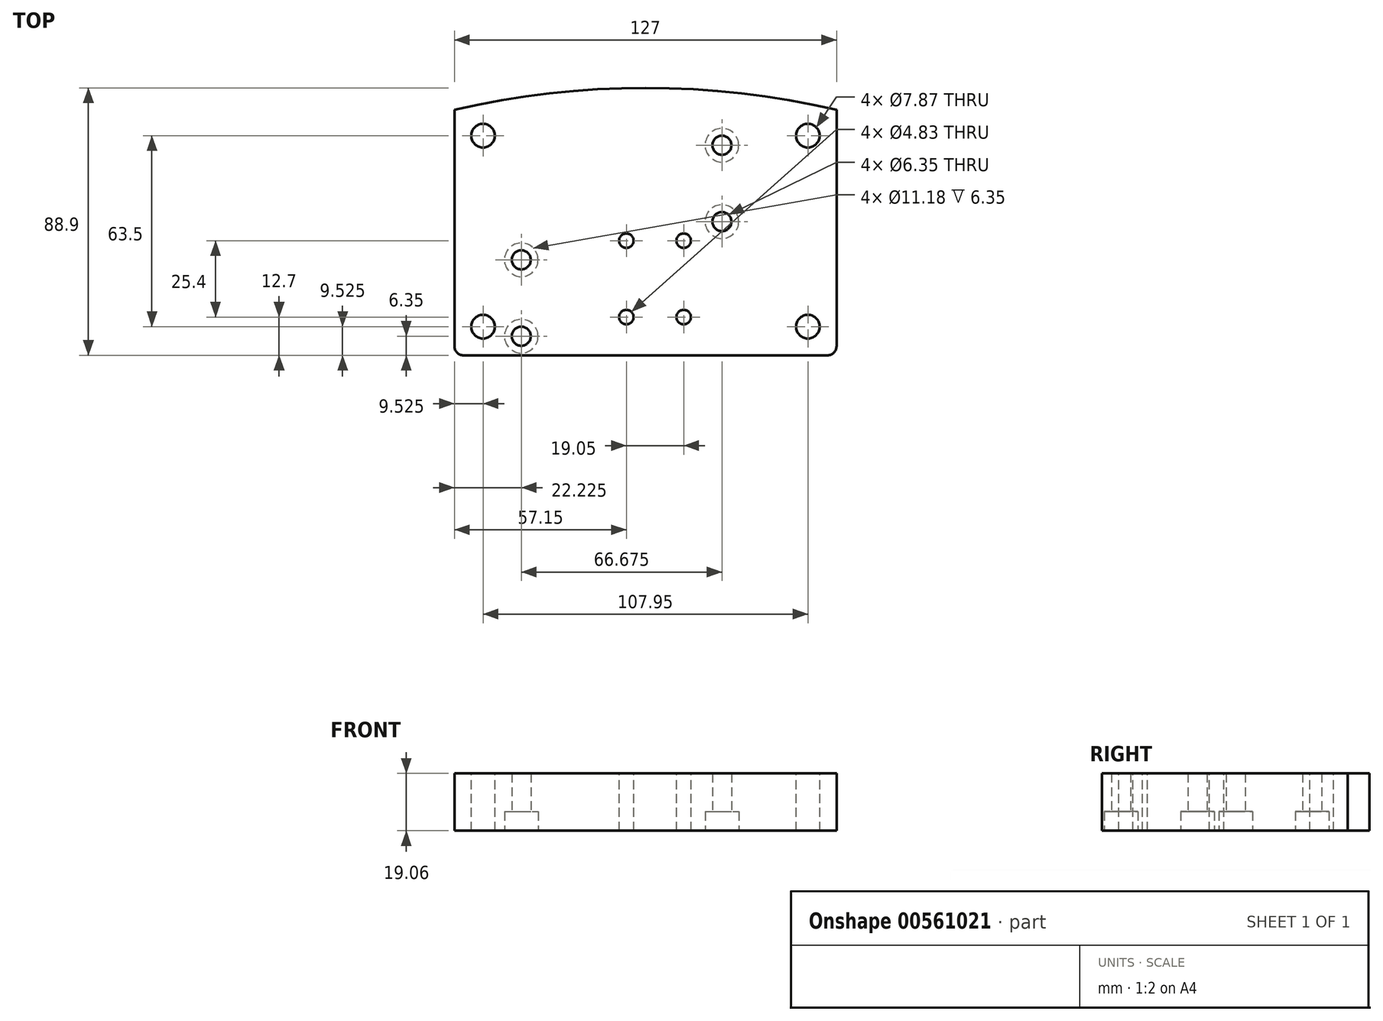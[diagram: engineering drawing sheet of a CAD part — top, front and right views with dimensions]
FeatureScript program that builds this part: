
annotation { "Feature Type Name" : "Feature", "Feature Type Description" : "" }
export const myFeature = defineFeature(function(context is Context, id is Id, definition is map)
    precondition{}
    {
        {
            var Q0;
            Q0=qCreatedBy(makeId("Front.planeOp"),FACE);
            var sketch = newSketch(context, id + "F0", { "sketchPlane" : qUnion([Q0])});
            skLineSegment(sketch, "E0", {"start": v(0, 82.23) * mm, "end": v(0, -82.23) * mm, "construction": true});
            skPoint(sketch, "E1", {"position": v(0, 0) * mm});
            skLineSegment(sketch, "E2.bottom", {"start": v(63.5, -9.52) * mm, "end": v(-63.5, -9.52) * mm});
            skLineSegment(sketch, "E2.top", {"start": v(63.5, 9.53) * mm, "end": v(-63.5, 9.53) * mm});
            skLineSegment(sketch, "E2.left", {"start": v(63.5, -9.52) * mm, "end": v(63.5, 9.53) * mm});
            skLineSegment(sketch, "E2.right", {"start": v(-63.5, -9.52) * mm, "end": v(-63.5, 9.53) * mm});
            skSolve(sketch);
        }
        {
            var Q0;
            Q0 = qSketchRegion(id + "F0", true);
            extrude(context, id + "F1", {"entities" : qUnion([Q0]), "oppositeDirection" : true, "depth" : 88.9 * mm, "offsetDistance" : 25.4 * mm});
        }
        {
            var Q0;
            Q0=makeQuery(id+"F1.opExtrude","SWEPT_FACE",FACE,{"disambiguationData":[OSD([sQuery(id+"F0.wireOp",EDGE,"E2.top")])]});
            var sketch = newSketch(context, id + "F2", { "sketchPlane" : qUnion([Q0])});
            skCircle(sketch, "E3", {"center": v(53.98, 73.03) * mm, "radius": 3.94 * mm});
            skCircle(sketch, "E4", {"center": v(-53.97, 73.03) * mm, "radius": 3.94 * mm});
            skLineSegment(sketch, "E5", {"start": v(0, 104.73) * mm, "end": v(0, -104.73) * mm, "construction": true});
            skPoint(sketch, "E6", {"position": v(0, 0) * mm});
            skCircle(sketch, "E7", {"center": v(53.98, 9.53) * mm, "radius": 3.94 * mm});
            skCircle(sketch, "E8", {"center": v(-53.97, 9.53) * mm, "radius": 3.94 * mm});
            skCircle(sketch, "E9", {"center": v(-6.35, 38.1) * mm, "radius": 2.41 * mm});
            skCircle(sketch, "E10", {"center": v(-6.35, 12.7) * mm, "radius": 2.41 * mm});
            skCircle(sketch, "E11", {"center": v(12.7, 38.1) * mm, "radius": 2.41 * mm});
            skCircle(sketch, "E12", {"center": v(12.7, 12.7) * mm, "radius": 2.41 * mm});
            skLineSegment(sketch, "E13", {"start": v(-53.97, 100.57) * mm, "end": v(-53.97, -13.49) * mm, "construction": true});
            skLineSegment(sketch, "E14", {"start": v(53.98, 101.03) * mm, "end": v(53.98, -14.64) * mm, "construction": true});
            skLineSegment(sketch, "E15", {"start": v(-74.16, 9.53) * mm, "end": v(79.92, 9.53) * mm, "construction": true});
            skLineSegment(sketch, "E16", {"start": v(-71.38, 73.03) * mm, "end": v(67.43, 73.03) * mm, "construction": true});
            skLineSegment(sketch, "E17", {"start": v(-6.35, 54.76) * mm, "end": v(-6.35, 2.48) * mm, "construction": true});
            skLineSegment(sketch, "E18", {"start": v(12.7, 53.6) * mm, "end": v(12.7, -1.92) * mm, "construction": true});
            skSolve(sketch);
        }
        {
            var Q0;
            Q0=makeQuery(id+"F2.imprint","IMPRINT",FACE,{"disambiguationData":[TD([[makeQuery(id+"F2.imprint","IMPRINT",EDGE,{"derivedFrom":sQuery(id+"F2.wireOp",EDGE,"E4")}),1.0]])]});
            var Q1;
            Q1=makeQuery(id+"F2.imprint","IMPRINT",FACE,{"disambiguationData":[TD([[makeQuery(id+"F2.imprint","IMPRINT",EDGE,{"derivedFrom":sQuery(id+"F2.wireOp",EDGE,"E8")}),1.0]])]});
            var Q2;
            Q2=makeQuery(id+"F2.imprint","IMPRINT",FACE,{"disambiguationData":[TD([[makeQuery(id+"F2.imprint","IMPRINT",EDGE,{"derivedFrom":sQuery(id+"F2.wireOp",EDGE,"E7")}),1.0]])]});
            var Q3;
            Q3=makeQuery(id+"F2.imprint","IMPRINT",FACE,{"disambiguationData":[TD([[makeQuery(id+"F2.imprint","IMPRINT",EDGE,{"derivedFrom":sQuery(id+"F2.wireOp",EDGE,"E3")}),1.0]])]});
            var Q4;
            Q4=makeQuery(id+"F2.imprint","IMPRINT",FACE,{"disambiguationData":[TD([[makeQuery(id+"F2.imprint","IMPRINT",EDGE,{"derivedFrom":sQuery(id+"F2.wireOp",EDGE,"E9")}),1.0]])]});
            var Q5;
            Q5=makeQuery(id+"F2.imprint","IMPRINT",FACE,{"disambiguationData":[TD([[makeQuery(id+"F2.imprint","IMPRINT",EDGE,{"derivedFrom":sQuery(id+"F2.wireOp",EDGE,"E11")}),1.0]])]});
            var Q6;
            Q6=makeQuery(id+"F2.imprint","IMPRINT",FACE,{"disambiguationData":[TD([[makeQuery(id+"F2.imprint","IMPRINT",EDGE,{"derivedFrom":sQuery(id+"F2.wireOp",EDGE,"E12")}),1.0]])]});
            var Q7;
            Q7=makeQuery(id+"F2.imprint","IMPRINT",FACE,{"disambiguationData":[TD([[makeQuery(id+"F2.imprint","IMPRINT",EDGE,{"derivedFrom":sQuery(id+"F2.wireOp",EDGE,"E10")}),1.0]])]});
            extrude(context, id + "F3", {"entities" : qUnion([Q0, Q1, Q2, Q3, Q4, Q5, Q6, Q7]), "operationType" : NewBodyOperationType.REMOVE, "endBound" : BoundingType.UP_TO_NEXT, "oppositeDirection" : true, "depth" : 25.4 * mm, "offsetDistance" : 25.4 * mm});
        }
        {
            var Q0;
            Q0=makeQuery(id+"F1.opExtrude","SWEPT_FACE",FACE,{"disambiguationData":[OSD([sQuery(id+"F0.wireOp",EDGE,"E2.bottom")])]});
            var sketch = newSketch(context, id + "F4", { "sketchPlane" : qUnion([Q0])});
            skCircle(sketch, "E19", {"center": v(25.4, -69.85) * mm, "radius": 3.18 * mm});
            skCircle(sketch, "E20", {"center": v(25.4, -44.45) * mm, "radius": 3.18 * mm});
            skCircle(sketch, "E21", {"center": v(-41.27, -31.75) * mm, "radius": 3.18 * mm});
            skCircle(sketch, "E22", {"center": v(-41.27, -6.35) * mm, "radius": 3.18 * mm});
            skLineSegment(sketch, "E23", {"start": v(42.34, -69.85) * mm, "end": v(10.41, -69.85) * mm, "construction": true});
            skLineSegment(sketch, "E24", {"start": v(40.26, -44.45) * mm, "end": v(10.87, -44.45) * mm, "construction": true});
            skLineSegment(sketch, "E25", {"start": v(-28.23, -31.75) * mm, "end": v(-53.67, -31.75) * mm, "construction": true});
            skLineSegment(sketch, "E26", {"start": v(-27.53, -6.35) * mm, "end": v(-56.3, -6.35) * mm, "construction": true});
            skSolve(sketch);
        }
        {
            var Q0;
            Q0=sQuery(id+"F4.wireOp",VERTEX,"E19.center");
            var Q1;
            Q1=sQuery(id+"F4.wireOp",VERTEX,"E20.center");
            var Q2;
            Q2=sQuery(id+"F4.wireOp",VERTEX,"E21.center");
            var Q3;
            Q3=sQuery(id+"F4.wireOp",VERTEX,"E22.center");
            var Q4;
            Q4=makeQuery(id+"F1.opExtrude","SWEPT_BODY",BODY,{"disambiguationData":[OSD([sQuery(id+"F0.wireOp",EDGE,"E2.bottom"),sQuery(id+"F0.wireOp",EDGE,"E2.top"),sQuery(id+"F0.wireOp",EDGE,"E2.left"),sQuery(id+"F0.wireOp",EDGE,"E2.right")])]});
            hole(context, id + "F5", {"style" : HoleStyle.C_BORE, "endStyle" : HoleEndStyle.THROUGH, "holeDiameter" : 6.35 * mm, "cBoreDiameter" : 11.18 * mm, "cBoreDepth" : 6.35 * mm, "isTappedThrough" : true, "tappedDepth" : 12.7 * mm, "tapClearance" : 3, "startFromSketch" : true, "locations" : qUnion([Q0, Q1, Q2, Q3]), "scope" : qUnion([Q4])});
        }
        {
            var Q0;
            Q0=makeQuery(id+"F4.imprint","IMPRINT",FACE,{"disambiguationData":[TD([[makeQuery(id+"F4.imprint","IMPRINT",EDGE,{"derivedFrom":sQuery(id+"F4.wireOp",EDGE,"E19")}),-1.0]])]});
            var sketch = newSketch(context, id + "F6", { "sketchPlane" : qUnion([Q0])});
            skArc(sketch, "E27", {"start": v(-63.5, -81.59) * mm, "mid": v(0, -88.9) * mm, "end": v(63.5, -81.59) * mm});
            skPoint(sketch, "E28", {"position": v(0, -88.9) * mm});
            skLineSegment(sketch, "E29", {"start": v(63.5, -81.59) * mm, "end": v(63.5, -94.2) * mm});
            skLineSegment(sketch, "E30", {"start": v(63.5, -94.2) * mm, "end": v(-63.5, -94.2) * mm});
            skLineSegment(sketch, "E31", {"start": v(-63.5, -94.2) * mm, "end": v(-63.5, -81.59) * mm});
            skSolve(sketch);
        }
        {
            var Q0;
            Q0 = qSketchRegion(id + "F6", true);
            extrude(context, id + "F7", {"entities" : qUnion([Q0]), "operationType" : NewBodyOperationType.REMOVE, "endBound" : BoundingType.THROUGH_ALL, "oppositeDirection" : true, "depth" : 25.4 * mm, "offsetDistance" : 25.4 * mm});
        }
        {
            var Q0;
            Q0=makeQuery(id+"F7.boolean.opBoolean","COPY",EDGE,{"derivedFrom":makeQuery(id+"F7.opExtrude","SWEPT_EDGE",EDGE,{"disambiguationData":[OSD([sQuery(id+"F0.wireOp",EDGE,"E2.bottom"),sQuery(id+"F0.wireOp",EDGE,"E2.left"),sQuery(id+"F6.wireOp",EDGE,"E27"),sQuery(id+"F6.wireOp",EDGE,"E29")])]})});
            var Q1;
            Q1=makeQuery(id+"F1.opExtrude","CAP_EDGE",EDGE,{"disambiguationData":[OSD([sQuery(id+"F0.wireOp",EDGE,"E2.left")])],"isStart":true});
            var Q2;
            Q2=makeQuery(id+"F7.boolean.opBoolean","COPY",EDGE,{"derivedFrom":makeQuery(id+"F7.opExtrude","SWEPT_EDGE",EDGE,{"disambiguationData":[OSD([sQuery(id+"F0.wireOp",EDGE,"E2.bottom"),sQuery(id+"F0.wireOp",EDGE,"E2.right"),sQuery(id+"F6.wireOp",EDGE,"E27"),sQuery(id+"F6.wireOp",EDGE,"E31")])]})});
            var Q3;
            Q3=makeQuery(id+"F1.opExtrude","CAP_EDGE",EDGE,{"disambiguationData":[OSD([sQuery(id+"F0.wireOp",EDGE,"E2.right")])],"isStart":true});
            fillet(context, id + "F8", {"entities" : qUnion([Q0, Q1, Q2, Q3]), "radius" : 3.05 * mm, "tangentPropagation" : true, "allowEdgeOverflow" : false});
        }
    });
